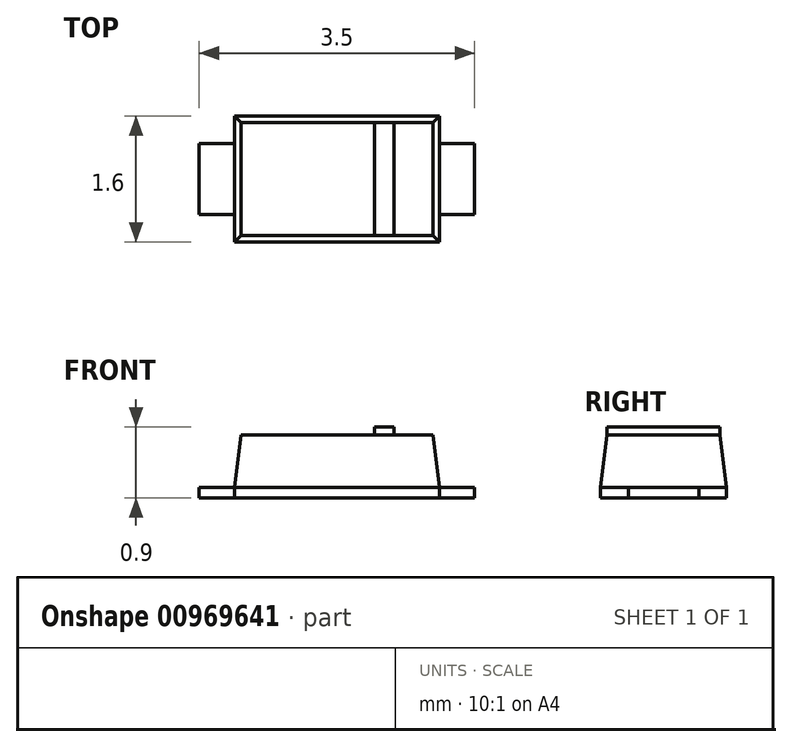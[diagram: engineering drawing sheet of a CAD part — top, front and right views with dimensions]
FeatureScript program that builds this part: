
annotation { "Feature Type Name" : "Feature", "Feature Type Description" : "" }
export const myFeature = defineFeature(function(context is Context, id is Id, definition is map)
    precondition{}
    {
        {
            var Q0;
            Q0=qCreatedBy(makeId("Top.planeOp"),FACE);
            var sketch = newSketch(context, id + "F0", { "sketchPlane" : qUnion([Q0])});
            skLineSegment(sketch, "E0.bottom", {"start": v(-1.3, -0.45) * mm, "end": v(-1.75, -0.45) * mm});
            skLineSegment(sketch, "E0.top", {"start": v(-1.3, 0.45) * mm, "end": v(-1.75, 0.45) * mm});
            skLineSegment(sketch, "E0.left", {"start": v(-1.3, -0.45) * mm, "end": v(-1.3, 0.45) * mm});
            skLineSegment(sketch, "E0.right", {"start": v(-1.75, -0.45) * mm, "end": v(-1.75, 0.45) * mm});
            skPoint(sketch, "E0.middle", {"position": v(-1.52, 0) * mm});
            skLineSegment(sketch, "E1.MirrorCS", {"start": v(1.3, 0.45) * mm, "end": v(1.75, 0.45) * mm});
            skLineSegment(sketch, "E2.MirrorCS", {"start": v(1.3, -0.45) * mm, "end": v(1.3, 0.45) * mm});
            skLineSegment(sketch, "E3.MirrorCS", {"start": v(1.3, -0.45) * mm, "end": v(1.75, -0.45) * mm});
            skLineSegment(sketch, "E4.MirrorCS", {"start": v(1.75, -0.45) * mm, "end": v(1.75, 0.45) * mm});
            skLineSegment(sketch, "E5.bottom", {"start": v(1.3, -0.8) * mm, "end": v(-1.3, -0.8) * mm});
            skLineSegment(sketch, "E5.top", {"start": v(1.3, 0.8) * mm, "end": v(-1.3, 0.8) * mm});
            skLineSegment(sketch, "E5.left", {"start": v(1.3, -0.8) * mm, "end": v(1.3, 0.8) * mm});
            skLineSegment(sketch, "E5.right", {"start": v(-1.3, -0.8) * mm, "end": v(-1.3, 0.8) * mm});
            skPoint(sketch, "E5.middle", {"position": v(0, 0) * mm});
            skSolve(sketch);
        }
        {
            var Q0;
            {var subQ0=sQuery(id+"F0.wireOp",EDGE,"E1.MirrorCS");Q0=makeQuery(id+"F0.imprint","IMPRINT",FACE,{"disambiguationData":[TD([[makeQuery(id+"F0.imprint","IMPRINT",EDGE,{"derivedFrom":subQ0}),-1.0]])]});}
            var Q1;
            {var subQ0=sQuery(id+"F0.wireOp",EDGE,"E0.bottom");Q1=makeQuery(id+"F0.imprint","IMPRINT",FACE,{"disambiguationData":[TD([[makeQuery(id+"F0.imprint","IMPRINT",EDGE,{"derivedFrom":subQ0}),-1.0]])]});}
            extrude(context, id + "F1", {"entities" : qUnion([Q0, Q1]), "depth" : .13 * mm, "offsetDistance" : 25 * mm});
        }
        {
            var Q0;
            {var subQ3=sQuery(id+"F0.wireOp",EDGE,"E5.bottom");Q0=makeQuery(id+"F0.imprint","IMPRINT",FACE,{"disambiguationData":[TD([[makeQuery(id+"F0.imprint","IMPRINT",EDGE,{"derivedFrom":subQ3}),-1.0]])]});}
            extrude(context, id + "F2", {"entities" : qUnion([Q0]), "depth" : .8 * mm, "offsetDistance" : 25 * mm});
        }
        {
            var Q0;
            Q0=makeQuery(id+"F2.opExtrude","CAP_FACE",FACE,{"disambiguationData":[OSD([sQuery(id+"F0.wireOp",EDGE,"E5.bottom"),sQuery(id+"F0.wireOp",EDGE,"E5.top"),sQuery(id+"F0.wireOp",EDGE,"E5.left"),sQuery(id+"F0.wireOp",EDGE,"E5.right")])],"isStart":false});
            chamfer(context, id + "F3", {"entities" : qUnion([Q0]), "chamferType" : ChamferType.OFFSET_ANGLE, "width" : .67 * mm, "oppositeDirection" : false, "angle" : 7 * degree, "tangentPropagation" : true});
        }
        {
            var Q0;
            Q0=makeQuery(id+"F2.opExtrude","CAP_FACE",FACE,{"disambiguationData":[OSD([sQuery(id+"F0.wireOp",EDGE,"E5.bottom"),sQuery(id+"F0.wireOp",EDGE,"E5.top"),sQuery(id+"F0.wireOp",EDGE,"E5.left"),sQuery(id+"F0.wireOp",EDGE,"E5.right")])],"isStart":false});
            var sketch = newSketch(context, id + "F4", { "sketchPlane" : qUnion([Q0])});
            skLineSegment(sketch, "E6.bottom", {"start": v(0.72, -0.72) * mm, "end": v(0.48, -0.72) * mm});
            skLineSegment(sketch, "E6.top", {"start": v(0.72, 0.72) * mm, "end": v(0.48, 0.72) * mm});
            skLineSegment(sketch, "E6.left", {"start": v(0.72, -0.72) * mm, "end": v(0.72, 0.72) * mm});
            skLineSegment(sketch, "E6.right", {"start": v(0.48, -0.72) * mm, "end": v(0.48, 0.72) * mm});
            skSolve(sketch);
        }
        {
            var Q0;
            Q0=makeQuery(id+"F4.imprint","IMPRINT",FACE,{"disambiguationData":[TD([[makeQuery(id+"F4.imprint","IMPRINT",EDGE,{"derivedFrom":sQuery(id+"F4.wireOp",EDGE,"E6.bottom")}),1.0]])]});
            extrude(context, id + "F5", {"entities" : qUnion([Q0]), "operationType" : NewBodyOperationType.ADD, "depth" : .1 * mm, "offsetDistance" : 25 * mm});
        }
    });
